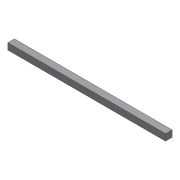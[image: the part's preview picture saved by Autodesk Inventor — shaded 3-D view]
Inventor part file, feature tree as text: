
AUTODESK INVENTOR PART (.ipt)
format: ipt  version: 2012 (Build 160160000, 160)  size: 73,216 bytes
history: native  units: in
note: dims shown in document units (in); Inventor stores cm internally (conversion verified against a paired STEP export)
features: extrude x1, sketch x1
ambient origin geometry x8: Origin, YZ Plane, XZ Plane, XY Plane, X Axis, Y Axis, Z Axis, Center Point
bodies: Solid1 (feature_tree)
feature tree (2):
  extrude  "Extrusion1"  Depth=23.0in
  sketch  "Sketch1"  dims[d0=1.0in d1=23.0in d2=0.25in d3=0.25in d4=0.5in d5=0.5in d6=6.0in d7=1.0in d8=0.0in]
